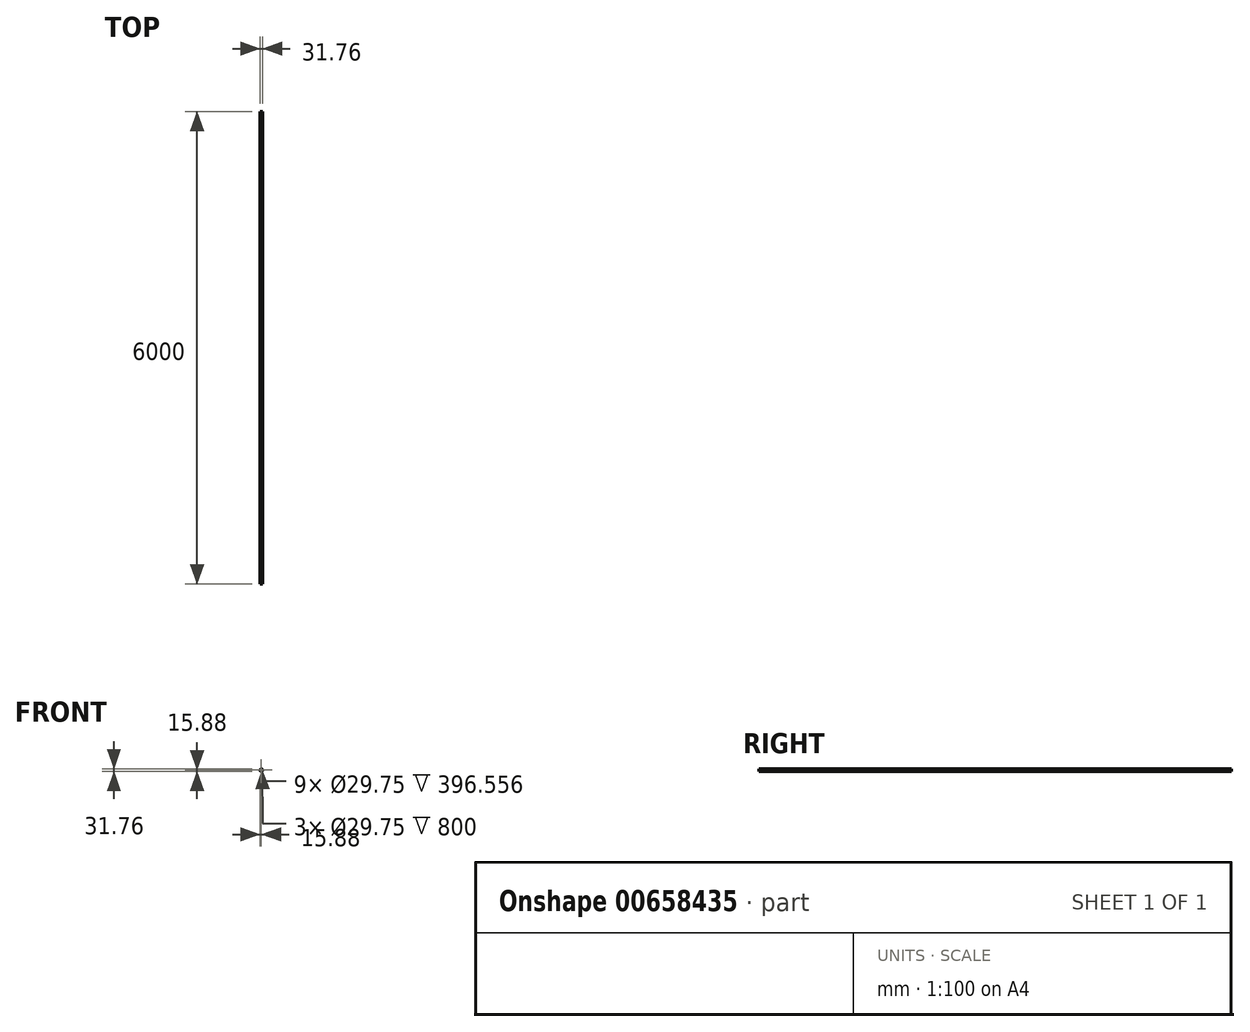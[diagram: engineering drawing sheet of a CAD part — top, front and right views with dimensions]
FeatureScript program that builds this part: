
annotation { "Feature Type Name" : "Feature", "Feature Type Description" : "" }
export const myFeature = defineFeature(function(context is Context, id is Id, definition is map)
    precondition{}
    {
        {
            var Q0;
            Q0=qCreatedBy(makeId("Front.planeOp"),FACE);
            var sketch = newSketch(context, id + "F0", { "sketchPlane" : qUnion([Q0])});
            skCircle(sketch, "E0", {"center": v(0, 0) * mm, "radius": 15.88 * mm});
            skCircle(sketch, "E1.0", {"center": v(0, 0) * mm, "radius": 14.88 * mm});
            skSolve(sketch);
        }
        {
            var Q0;
            Q0=makeQuery(id+"F0.imprint","IMPRINT",FACE,{"disambiguationData":[TD([[makeQuery(id+"F0.imprint","IMPRINT",EDGE,{"derivedFrom":sQuery(id+"F0.wireOp",EDGE,"E0")}),1.0]])]});
            extrude(context, id + "F1", {"entities" : qUnion([Q0]), "endBound" : BoundingType.SYMMETRIC, "depth" : 6000 * mm, "offsetDistance" : 25 * mm});
        }
        {
            var Q0;
            Q0=qCreatedBy(makeId("Top.planeOp"),FACE);
            var sketch = newSketch(context, id + "F2", { "sketchPlane" : qUnion([Q0])});
            skLineSegment(sketch, "E2.0", {"start": v(15.88, 3000) * mm, "end": v(-15.88, 3000) * mm, "construction": true});
            skLineSegment(sketch, "E3", {"start": v(-15.88, -3000) * mm, "end": v(-15.88, 3000) * mm, "construction": true});
            skLineSegment(sketch, "E4", {"start": v(15.88, 3000) * mm, "end": v(15.88, -3000) * mm, "construction": true});
            skLineSegment(sketch, "E5.0", {"start": v(15.88, -3000) * mm, "end": v(-15.88, -3000) * mm, "construction": true});
            skLineSegment(sketch, "E6.bottom", {"start": v(-15.88, -1001.33) * mm, "end": v(15.88, -1001.33) * mm});
            skLineSegment(sketch, "E6.top", {"start": v(-15.88, -999.33) * mm, "end": v(15.88, -999.33) * mm});
            skLineSegment(sketch, "E6.left", {"start": v(-15.88, -1001.33) * mm, "end": v(-15.88, -999.33) * mm});
            skLineSegment(sketch, "E6.right", {"start": v(15.88, -1001.33) * mm, "end": v(15.88, -999.33) * mm});
            skLineSegment(sketch, "E7.bottom", {"start": v(-15.88, 999.33) * mm, "end": v(15.88, 999.33) * mm});
            skLineSegment(sketch, "E7.top", {"start": v(-15.88, 1001.33) * mm, "end": v(15.88, 1001.33) * mm});
            skLineSegment(sketch, "E7.left", {"start": v(-15.88, 999.33) * mm, "end": v(-15.88, 1001.33) * mm});
            skLineSegment(sketch, "E7.right", {"start": v(15.88, 999.33) * mm, "end": v(15.88, 1001.33) * mm});
            skLineSegment(sketch, "E8", {"start": v(15.88, -3000) * mm, "end": v(15.88, -1001.33) * mm, "construction": true});
            skLineSegment(sketch, "E9", {"start": v(15.88, -999.33) * mm, "end": v(15.88, 999.33) * mm, "construction": true});
            skLineSegment(sketch, "E10", {"start": v(15.88, 1001.33) * mm, "end": v(15.88, 3000) * mm, "construction": true});
            skSolve(sketch);
        }
        {
            var Q0;
            Q0 = qSketchRegion(id + "F2", true);
            extrude(context, id + "F3", {"entities" : qUnion([Q0]), "operationType" : NewBodyOperationType.REMOVE, "endBound" : BoundingType.SYMMETRIC, "oppositeDirection" : true, "depth" : 32 * mm, "offsetDistance" : 25 * mm});
        }
        {
            var Q0;
            Q0=qCreatedBy(makeId("Top.planeOp"),FACE);
            var sketch = newSketch(context, id + "F4", { "sketchPlane" : qUnion([Q0])});
            skLineSegment(sketch, "E11.0", {"start": v(15.88, -3000) * mm, "end": v(-15.88, -3000) * mm, "construction": true});
            skLineSegment(sketch, "E12.bottom", {"start": v(-15.88, -2200) * mm, "end": v(15.87, -2200) * mm});
            skLineSegment(sketch, "E12.top", {"start": v(-15.88, -2197) * mm, "end": v(15.87, -2197) * mm});
            skLineSegment(sketch, "E12.left", {"start": v(-15.88, -2200) * mm, "end": v(-15.88, -2197) * mm});
            skLineSegment(sketch, "E12.right", {"start": v(15.87, -2200) * mm, "end": v(15.87, -2197) * mm});
            skLineSegment(sketch, "E13", {"start": v(-15.87, -3000) * mm, "end": v(-15.87, -2200) * mm, "construction": true});
            skLineSegment(sketch, "E14.bottom", {"start": v(-15.88, -1800.44) * mm, "end": v(15.87, -1800.44) * mm});
            skLineSegment(sketch, "E14.top", {"start": v(-15.88, -1797.44) * mm, "end": v(15.87, -1797.44) * mm});
            skLineSegment(sketch, "E14.left", {"start": v(-15.88, -1800.44) * mm, "end": v(-15.88, -1797.44) * mm});
            skLineSegment(sketch, "E14.right", {"start": v(15.87, -1800.44) * mm, "end": v(15.87, -1797.44) * mm});
            skLineSegment(sketch, "E15.bottom", {"start": v(-15.88, -1400.89) * mm, "end": v(15.87, -1400.89) * mm});
            skLineSegment(sketch, "E15.top", {"start": v(-15.88, -1397.89) * mm, "end": v(15.87, -1397.89) * mm});
            skLineSegment(sketch, "E15.left", {"start": v(-15.88, -1400.89) * mm, "end": v(-15.88, -1397.89) * mm});
            skLineSegment(sketch, "E15.right", {"start": v(15.87, -1400.89) * mm, "end": v(15.87, -1397.89) * mm});
            skLineSegment(sketch, "E16", {"start": v(-15.88, -2197) * mm, "end": v(-15.88, -1800.44) * mm, "construction": true});
            skLineSegment(sketch, "E17", {"start": v(-15.88, -1797.44) * mm, "end": v(-15.88, -1400.89) * mm, "construction": true});
            skLineSegment(sketch, "E18.0", {"start": v(15.88, -1001.33) * mm, "end": v(-15.88, -1001.33) * mm, "construction": true});
            skLineSegment(sketch, "E19.0", {"start": v(15.88, -999.33) * mm, "end": v(-15.88, -999.33) * mm, "construction": true});
            skLineSegment(sketch, "E20", {"start": v(-15.88, -1397.89) * mm, "end": v(-15.88, -1001.33) * mm, "construction": true});
            skLineSegment(sketch, "E21.bottom", {"start": v(-15.88, -199.33) * mm, "end": v(15.87, -199.33) * mm});
            skLineSegment(sketch, "E21.top", {"start": v(-15.88, -196.33) * mm, "end": v(15.87, -196.33) * mm});
            skLineSegment(sketch, "E21.left", {"start": v(-15.88, -199.33) * mm, "end": v(-15.88, -196.33) * mm});
            skLineSegment(sketch, "E21.right", {"start": v(15.87, -199.33) * mm, "end": v(15.87, -196.33) * mm});
            skLineSegment(sketch, "E22.bottom", {"start": v(-15.87, 200.22) * mm, "end": v(15.87, 200.22) * mm});
            skLineSegment(sketch, "E22.top", {"start": v(-15.87, 203.22) * mm, "end": v(15.87, 203.22) * mm});
            skLineSegment(sketch, "E22.left", {"start": v(-15.87, 200.22) * mm, "end": v(-15.87, 203.22) * mm});
            skLineSegment(sketch, "E22.right", {"start": v(15.87, 200.22) * mm, "end": v(15.87, 203.22) * mm});
            skLineSegment(sketch, "E23.bottom", {"start": v(-15.88, 599.78) * mm, "end": v(15.87, 599.78) * mm});
            skLineSegment(sketch, "E23.top", {"start": v(-15.88, 602.78) * mm, "end": v(15.87, 602.78) * mm});
            skLineSegment(sketch, "E23.left", {"start": v(-15.87, 599.78) * mm, "end": v(-15.87, 602.78) * mm});
            skLineSegment(sketch, "E23.right", {"start": v(15.87, 599.78) * mm, "end": v(15.87, 602.78) * mm});
            skLineSegment(sketch, "E24.0", {"start": v(15.88, 999.33) * mm, "end": v(-15.88, 999.33) * mm, "construction": true});
            skLineSegment(sketch, "E25.0", {"start": v(15.88, 1001.33) * mm, "end": v(-15.88, 1001.33) * mm, "construction": true});
            skLineSegment(sketch, "E26", {"start": v(-15.88, -999.33) * mm, "end": v(-15.88, -199.33) * mm, "construction": true});
            skLineSegment(sketch, "E27", {"start": v(-15.87, -196.33) * mm, "end": v(-15.87, 200.22) * mm, "construction": true});
            skLineSegment(sketch, "E28", {"start": v(-15.88, 203.22) * mm, "end": v(-15.88, 599.78) * mm, "construction": true});
            skLineSegment(sketch, "E29", {"start": v(-15.88, 602.78) * mm, "end": v(-15.88, 999.33) * mm, "construction": true});
            skLineSegment(sketch, "E30.bottom", {"start": v(-15.88, 1801.33) * mm, "end": v(15.87, 1801.33) * mm});
            skLineSegment(sketch, "E30.top", {"start": v(-15.88, 1804.33) * mm, "end": v(15.87, 1804.33) * mm});
            skLineSegment(sketch, "E30.left", {"start": v(-15.88, 1801.33) * mm, "end": v(-15.88, 1804.33) * mm});
            skLineSegment(sketch, "E30.right", {"start": v(15.87, 1801.33) * mm, "end": v(15.87, 1804.33) * mm});
            skLineSegment(sketch, "E31.bottom", {"start": v(-15.88, 2200.89) * mm, "end": v(15.87, 2200.89) * mm});
            skLineSegment(sketch, "E31.top", {"start": v(-15.87, 2203.89) * mm, "end": v(15.87, 2203.89) * mm});
            skLineSegment(sketch, "E31.left", {"start": v(-15.88, 2200.89) * mm, "end": v(-15.88, 2203.89) * mm});
            skLineSegment(sketch, "E31.right", {"start": v(15.87, 2200.89) * mm, "end": v(15.87, 2203.89) * mm});
            skLineSegment(sketch, "E32.bottom", {"start": v(-15.87, 2600.44) * mm, "end": v(15.87, 2600.44) * mm});
            skLineSegment(sketch, "E32.top", {"start": v(-15.87, 2603.44) * mm, "end": v(15.87, 2603.44) * mm});
            skLineSegment(sketch, "E32.left", {"start": v(-15.88, 2600.44) * mm, "end": v(-15.88, 2603.44) * mm});
            skLineSegment(sketch, "E32.right", {"start": v(15.87, 2600.44) * mm, "end": v(15.87, 2603.44) * mm});
            skLineSegment(sketch, "E33", {"start": v(-15.88, 1001.33) * mm, "end": v(-15.88, 1801.33) * mm, "construction": true});
            skLineSegment(sketch, "E34", {"start": v(-15.88, 1804.33) * mm, "end": v(-15.88, 2200.89) * mm, "construction": true});
            skLineSegment(sketch, "E35", {"start": v(-15.87, 2600.44) * mm, "end": v(-15.87, 2203.89) * mm, "construction": true});
            skLineSegment(sketch, "E36", {"start": v(-15.87, 2603.44) * mm, "end": v(-15.87, 3000) * mm, "construction": true});
            skLineSegment(sketch, "E37.0", {"start": v(15.88, 3000) * mm, "end": v(-15.88, 3000) * mm, "construction": true});
            skSolve(sketch);
        }
        {
            var Q0;
            Q0 = qSketchRegion(id + "F4", true);
            extrude(context, id + "F5", {"entities" : qUnion([Q0]), "operationType" : NewBodyOperationType.REMOVE, "endBound" : BoundingType.SYMMETRIC, "oppositeDirection" : true, "depth" : 35 * mm, "offsetDistance" : 25 * mm});
        }
    });
